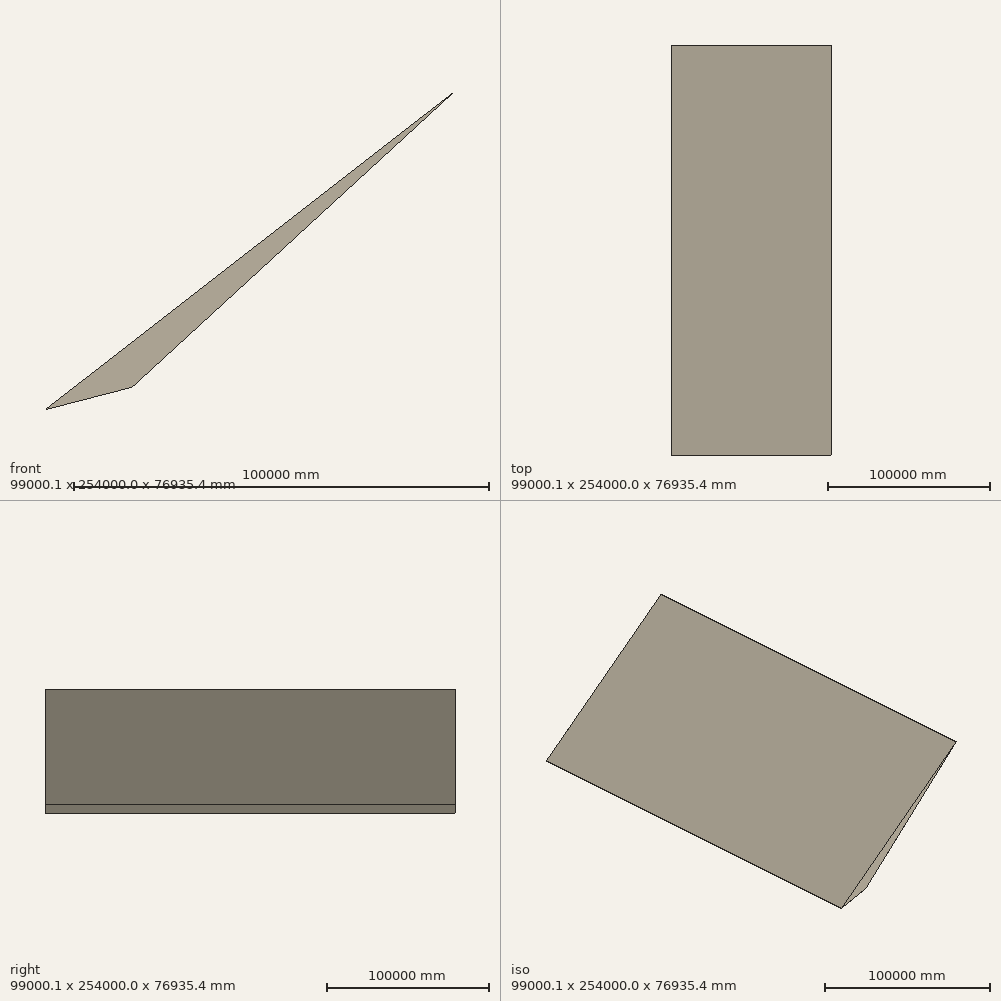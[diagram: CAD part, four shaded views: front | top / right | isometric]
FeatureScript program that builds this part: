
annotation { "Feature Type Name" : "Feature", "Feature Type Description" : "" }
export const myFeature = defineFeature(function(context is Context, id is Id, definition is map)
    precondition{}
    {
        {
            var Q0;
            Q0=qCreatedBy(makeId("Front.planeOp"),FACE);
            var sketch = newSketch(context, id + "F0", { "sketchPlane" : qUnion([Q0])});
            skLineSegment(sketch, "E0", {"start": v(-18208.86, -7255.4) * mm, "end": v(2818.38, -1801.7) * mm});
            skLineSegment(sketch, "E1", {"start": v(2818.38, -1801.7) * mm, "end": v(80791.2, 69680.03) * mm});
            skLineSegment(sketch, "E2", {"start": v(80791.2, 69680.03) * mm, "end": v(-18208.86, -7255.4) * mm});
            skSolve(sketch);
        }
        {
            var Q0;
            Q0=makeQuery(id+"F0.imprint","IMPRINT",FACE,{"disambiguationData":[TD([[makeQuery(id+"F0.imprint","IMPRINT",EDGE,{"derivedFrom":sQuery(id+"F0.wireOp",EDGE,"E0")}),1.0]])]});
            extrude(context, id + "F1", {"entities" : qUnion([Q0]), "depth" : 254000 * mm, "offsetDistance" : 25.4 * mm});
        }
    });
